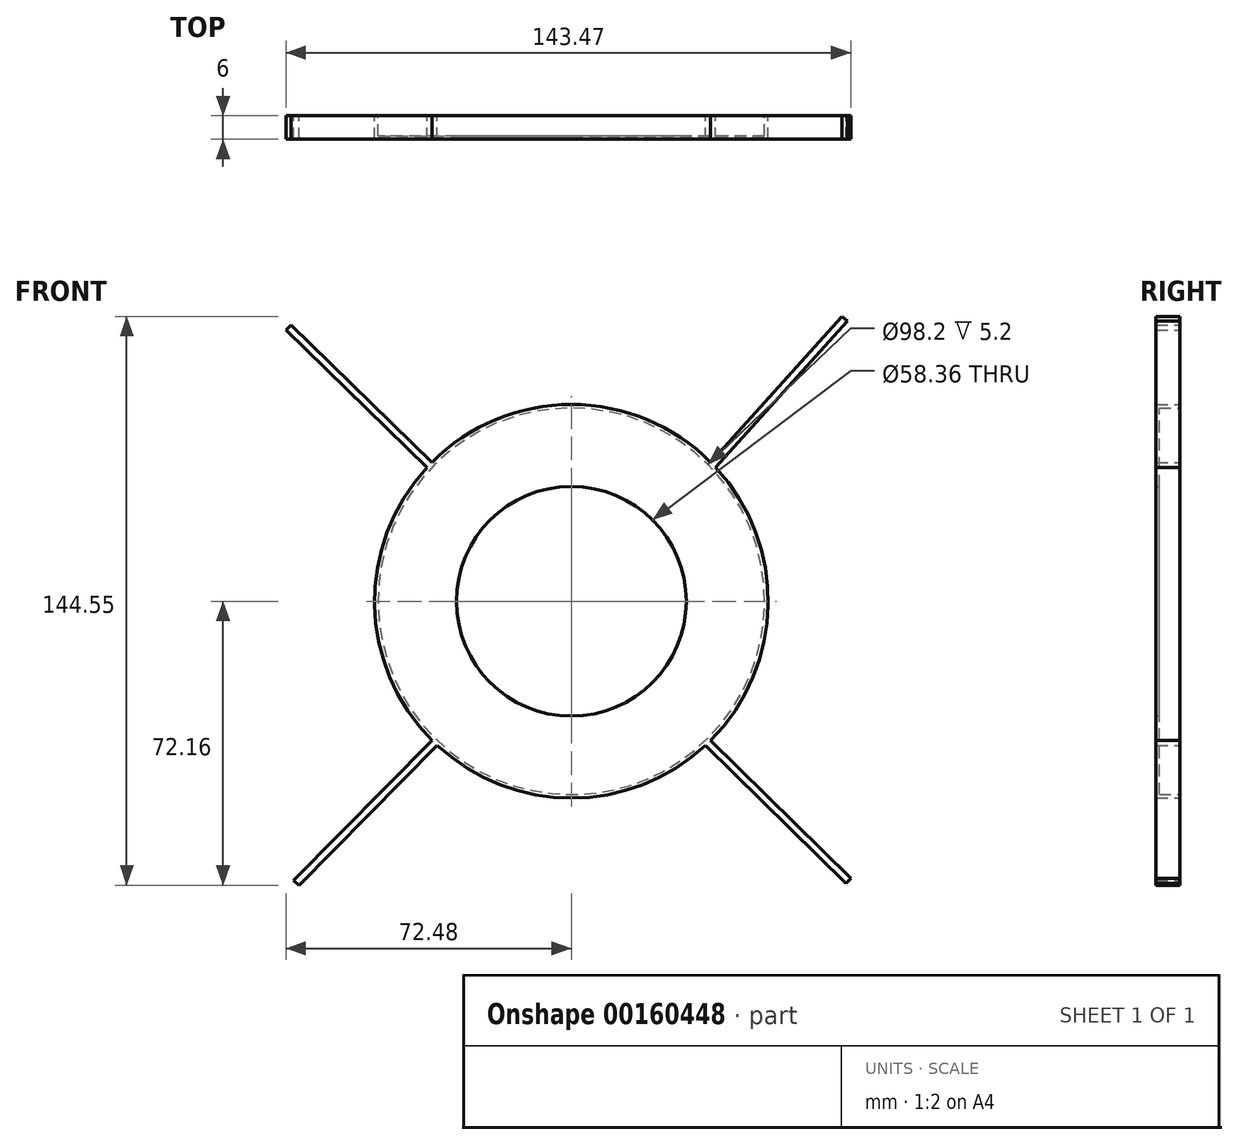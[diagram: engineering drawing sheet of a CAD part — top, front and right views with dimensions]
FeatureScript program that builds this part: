
annotation { "Feature Type Name" : "Feature", "Feature Type Description" : "" }
export const myFeature = defineFeature(function(context is Context, id is Id, definition is map)
    precondition{}
    {
        {
            var Q0;
            Q0=qCreatedBy(makeId("Front.planeOp"),FACE);
            var sketch = newSketch(context, id + "F0", { "sketchPlane" : qUnion([Q0])});
            skCircle(sketch, "E0", {"center": v(0, 0) * mm, "radius": 50 * mm});
            skLineSegment(sketch, "E1.bottom", {"start": v(-35.4, 35.32) * mm, "end": v(35.4, 35.32) * mm});
            skLineSegment(sketch, "E1.top", {"start": v(-35.4, -35.32) * mm, "end": v(35.4, -35.32) * mm});
            skLineSegment(sketch, "E1.left", {"start": v(-35.4, 35.32) * mm, "end": v(-35.4, -35.32) * mm});
            skLineSegment(sketch, "E1.right", {"start": v(35.4, 35.32) * mm, "end": v(35.4, -35.32) * mm});
            skLineSegment(sketch, "E2", {"start": v(-35.4, 35.32) * mm, "end": v(-71.23, 70.17) * mm});
            skLineSegment(sketch, "E3", {"start": v(-71.23, 70.17) * mm, "end": v(-72.48, 68.88) * mm});
            skLineSegment(sketch, "E4", {"start": v(-72.48, 68.88) * mm, "end": v(-36.64, 34.02) * mm});
            skLineSegment(sketch, "E5", {"start": v(35.4, 35.32) * mm, "end": v(68.75, 72.4) * mm});
            skLineSegment(sketch, "E6", {"start": v(68.75, 72.4) * mm, "end": v(70.09, 71.19) * mm});
            skLineSegment(sketch, "E7", {"start": v(70.09, 71.19) * mm, "end": v(36.65, 34.02) * mm});
            skLineSegment(sketch, "E8", {"start": v(-35.4, -35.32) * mm, "end": v(-70.52, -70.9) * mm});
            skLineSegment(sketch, "E9", {"start": v(-70.52, -70.9) * mm, "end": v(-69.24, -72.16) * mm});
            skLineSegment(sketch, "E10", {"start": v(-69.24, -72.16) * mm, "end": v(-34.1, -36.57) * mm});
            skLineSegment(sketch, "E11", {"start": v(35.4, -35.32) * mm, "end": v(71, -70.37) * mm});
            skLineSegment(sketch, "E12", {"start": v(71, -70.37) * mm, "end": v(69.73, -71.65) * mm});
            skLineSegment(sketch, "E13", {"start": v(69.73, -71.65) * mm, "end": v(34.1, -36.57) * mm});
            skSolve(sketch);
        }
        {
            var Q0;
            Q0 = qSketchRegion(id + "F0", true);
            extrude(context, id + "F1", {"entities" : qUnion([Q0]), "depth" : 6 * mm});
        }
        {
            var Q0;
            Q0=qCreatedBy(makeId("Front.planeOp"),FACE);
            var sketch = newSketch(context, id + "F2", { "sketchPlane" : qUnion([Q0])});
            skCircle(sketch, "E14", {"center": v(0, 0) * mm, "radius": 49.1 * mm});
            skSolve(sketch);
        }
        {
            var Q0;
            Q0 = qSketchRegion(id + "F2", true);
            extrude(context, id + "F3", {"entities" : qUnion([Q0]), "operationType" : NewBodyOperationType.REMOVE, "depth" : 5.2 * mm});
        }
        {
            var Q0;
            Q0=qCreatedBy(makeId("Front.planeOp"),FACE);
            var sketch = newSketch(context, id + "F4", { "sketchPlane" : qUnion([Q0])});
            skCircle(sketch, "E15", {"center": v(0, 0) * mm, "radius": 29.18 * mm});
            skSolve(sketch);
        }
        {
            var Q0;
            Q0 = qSketchRegion(id + "F4", true);
            extrude(context, id + "F5", {"entities" : qUnion([Q0]), "operationType" : NewBodyOperationType.REMOVE, "depth" : 25 * mm});
        }
    });
